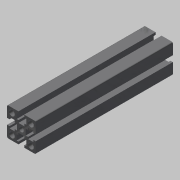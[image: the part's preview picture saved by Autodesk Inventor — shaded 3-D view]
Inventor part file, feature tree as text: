
AUTODESK INVENTOR PART (.ipt)
format: ipt  version: 2021.2 (Build 252289000, 289)  size: 205,312 bytes
history: native  units: in
note: dims shown in document units (in); Inventor stores cm internally (conversion verified against a paired STEP export)
features: other x2, extrude x1, sketch x1, projected_geometry x1
ambient origin geometry x8: Origin, YZ Plane, XZ Plane, XY Plane, X Axis, Y Axis, Z Axis, Center Point
bodies: Body1 (feature_tree)
feature tree (5):
  other  "ソリッド2"
  extrude  "押し出し1"  Depth=5.6693in
  sketch  "スケッチ2"
  projected_geometry  "投影ループ1"
  other  "ソリッド1"
